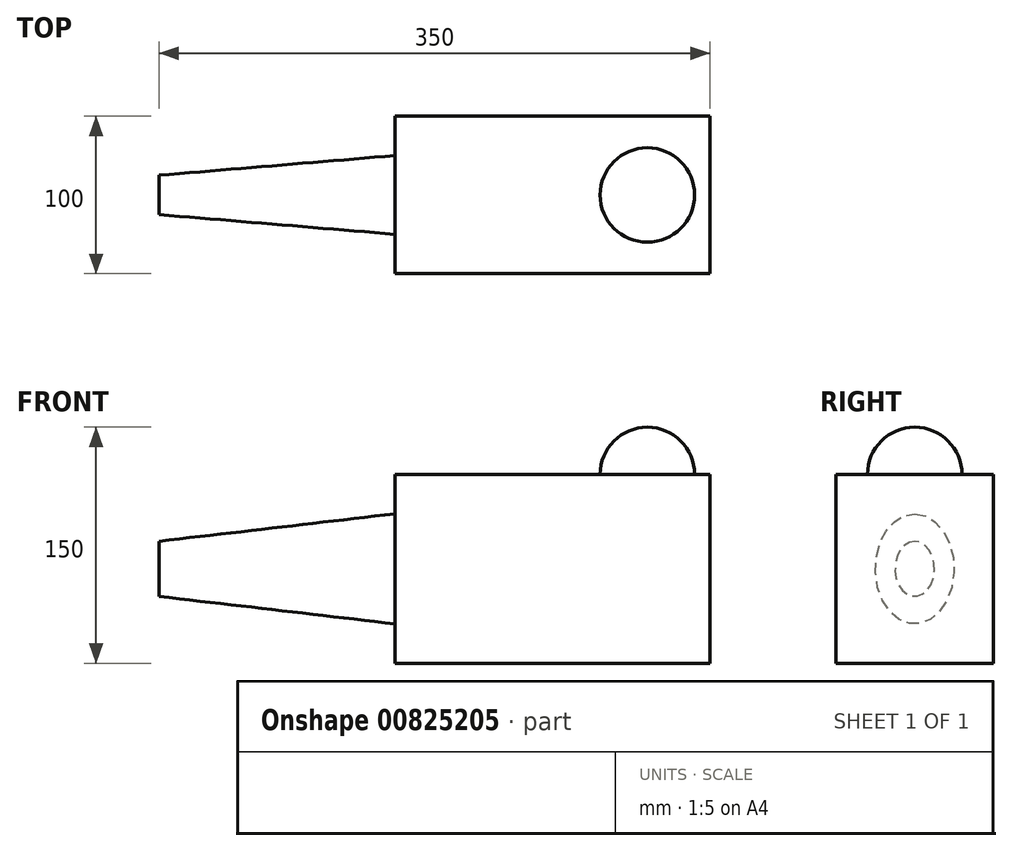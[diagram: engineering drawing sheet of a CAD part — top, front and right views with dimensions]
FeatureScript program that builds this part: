
annotation { "Feature Type Name" : "Feature", "Feature Type Description" : "" }
export const myFeature = defineFeature(function(context is Context, id is Id, definition is map)
    precondition{}
    {
        {
            var Q0;
            Q0=qCreatedBy(makeId("Top.planeOp"),FACE);
            var sketch = newSketch(context, id + "F0", { "sketchPlane" : qUnion([Q0])});
            skLineSegment(sketch, "E0.bottom", {"start": v(-100, 54.27) * mm, "end": v(100, 54.27) * mm});
            skLineSegment(sketch, "E0.top", {"start": v(-100, -45.73) * mm, "end": v(100, -45.73) * mm});
            skLineSegment(sketch, "E0.left", {"start": v(-100, 54.27) * mm, "end": v(-100, -45.73) * mm});
            skLineSegment(sketch, "E0.right", {"start": v(100, 54.27) * mm, "end": v(100, -45.73) * mm});
            skPoint(sketch, "E0.middle", {"position": v(0, 4.27) * mm});
            skSolve(sketch);
        }
        {
            var Q0;
            Q0 = qSketchRegion(id + "F0", true);
            extrude(context, id + "F1", {"entities" : qUnion([Q0]), "depth" : 120 * mm, "offsetDistance" : 25 * mm});
        }
        {
            var Q0;
            Q0=makeQuery(id+"F1.opExtrude","CAP_FACE",FACE,{"disambiguationData":[OSD([sQuery(id+"F0.wireOp",EDGE,"E0.bottom"),sQuery(id+"F0.wireOp",EDGE,"E0.top"),sQuery(id+"F0.wireOp",EDGE,"E0.left"),sQuery(id+"F0.wireOp",EDGE,"E0.right")])],"isStart":false});
            var sketch = newSketch(context, id + "F2", { "sketchPlane" : qUnion([Q0])});
            skLineSegment(sketch, "E1", {"start": v(-100, 4.27) * mm, "end": v(100, 4.27) * mm, "construction": true});
            skArc(sketch, "E2", {"start": v(60.17, -25.73) * mm, "mid": v(90.17, 4.27) * mm, "end": v(60.17, 34.27) * mm});
            skLineSegment(sketch, "E3", {"start": v(60.17, 4.27) * mm, "end": v(60.17, 34.27) * mm});
            skLineSegment(sketch, "E4", {"start": v(60.17, 34.27) * mm, "end": v(60.17, -25.73) * mm});
            skSolve(sketch);
        }
        {
            var Q0;
            {var subQ0=sQuery(id+"F2.wireOp",EDGE,"E2");Q0=makeQuery(id+"F2.imprint","IMPRINT",FACE,{"disambiguationData":[TD([[makeQuery(id+"F2.imprint","IMPRINT",EDGE,{"derivedFrom":subQ0}),1.0]])]});}
            var Q1;
            Q1=sQuery(id+"F2.wireOp",EDGE,"E4");
            revolve(context, id + "F3", {"operationType" : NewBodyOperationType.ADD, "surfaceOperationType" : NewSurfaceOperationType.NEW, "entities" : qUnion([Q0]), "axis" : qUnion([Q1]), "revolveType" : RevolveType.FULL});
        }
        {
            var Q0;
            Q0=makeQuery(id+"F1.opExtrude","SWEPT_FACE",FACE,{"disambiguationData":[OSD([sQuery(id+"F0.wireOp",EDGE,"E0.left")])]});
            var sketch = newSketch(context, id + "F4", { "sketchPlane" : qUnion([Q0])});
            skLineSegment(sketch, "E5", {"start": v(-4.27, 0) * mm, "end": v(-4.27, 120) * mm, "construction": true});
            skLineSegment(sketch, "E6", {"start": v(-54.27, 60) * mm, "end": v(45.73, 60) * mm, "construction": true});
            skEllipse(sketch, "E7", {"center": v(-4.27, 60) * mm, "majorRadius": 35 * mm, "minorRadius": 25 * mm, "majorAxis": v(0, 1)});
            skSolve(sketch);
        }
        {
            var Q0;
            Q0=qCreatedBy(makeId("Right.planeOp"),FACE);
            cPlane(context, id + "F5", {"entities" : qUnion([Q0]), "cplaneType" : CPlaneType.OFFSET, "offset" : 250 * mm, "oppositeDirection" : true, "width" : 150 * mm, "height" : 150 * mm});
        }
        {
            var Q0;
            Q0=qCreatedBy(id+"F5.planeOp",FACE);
            var sketch = newSketch(context, id + "F6", { "sketchPlane" : qUnion([Q0])});
            skEllipse(sketch, "E8", {"center": v(4.27, 60) * mm, "majorRadius": 17.5 * mm, "minorRadius": 12.5 * mm, "majorAxis": v(0, -1)});
            skSolve(sketch);
        }
        {
            var Q1;
            Q1=makeQuery(id+"F4.imprint","IMPRINT",FACE,{"disambiguationData":[TD([[makeQuery(id+"F4.imprint","IMPRINT",EDGE,{"derivedFrom":sQuery(id+"F4.wireOp",EDGE,"E7")}),1.0]])]});
            var Q2;
            Q2=makeQuery(id+"F6.imprint","IMPRINT",FACE,{"disambiguationData":[TD([[makeQuery(id+"F6.imprint","IMPRINT",EDGE,{"derivedFrom":sQuery(id+"F6.wireOp",EDGE,"E8")}),1.0]])]});
            loft(context, id + "F7", {"operationType" : NewBodyOperationType.ADD, "sheetProfilesArray" : [{ "sheetProfileEntities" : qUnion([Q1]) }, { "sheetProfileEntities" : qUnion([Q2]) }]});
        }
    });
